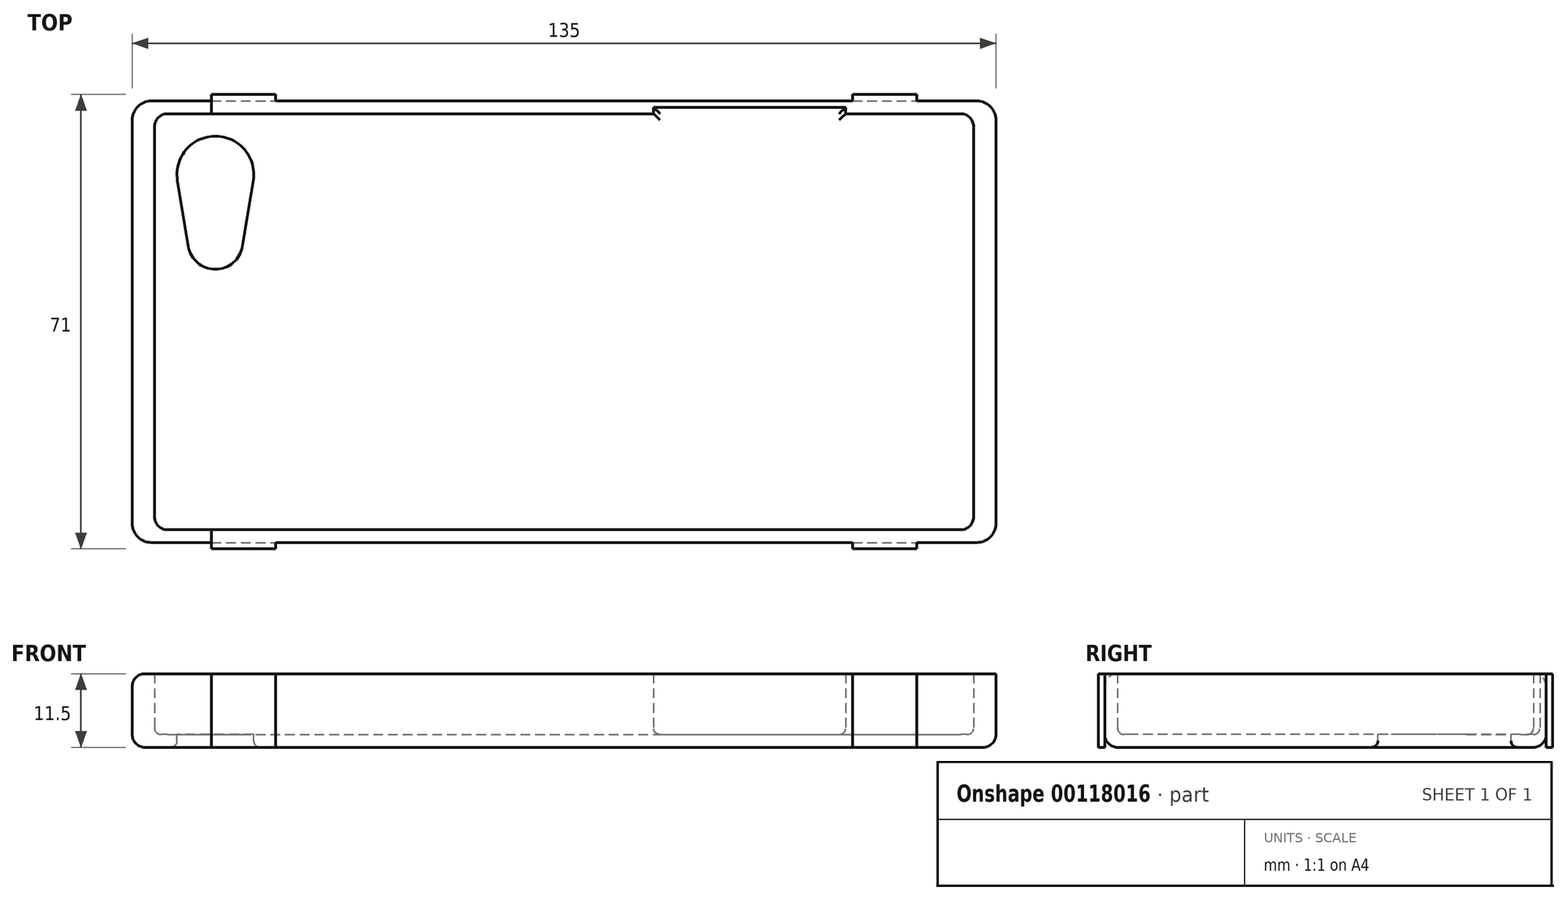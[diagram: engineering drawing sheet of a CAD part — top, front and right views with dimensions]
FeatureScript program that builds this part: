
annotation { "Feature Type Name" : "Feature", "Feature Type Description" : "" }
export const myFeature = defineFeature(function(context is Context, id is Id, definition is map)
    precondition{}
    {
        {
            var Q0;
            Q0=qCreatedBy(makeId("Top.planeOp"),FACE);
            var sketch = newSketch(context, id + "F0", { "sketchPlane" : qUnion([Q0])});
            skLineSegment(sketch, "E0.bottom", {"start": v(-67.5, 34.5) * mm, "end": v(67.5, 34.5) * mm});
            skLineSegment(sketch, "E0.top", {"start": v(-67.5, -34.5) * mm, "end": v(67.5, -34.5) * mm});
            skLineSegment(sketch, "E0.left", {"start": v(-67.5, 34.5) * mm, "end": v(-67.5, -34.5) * mm});
            skLineSegment(sketch, "E0.right", {"start": v(67.5, 34.5) * mm, "end": v(67.5, -34.5) * mm});
            skLineSegment(sketch, "E1.bottom", {"start": v(-64, 32.5) * mm, "end": v(14, 32.5) * mm});
            skLineSegment(sketch, "E1.top", {"start": v(-64, -32.5) * mm, "end": v(64, -32.5) * mm});
            skLineSegment(sketch, "E1.left", {"start": v(-64, 32.5) * mm, "end": v(-64, -32.5) * mm});
            skLineSegment(sketch, "E1.right", {"start": v(64, 32.5) * mm, "end": v(64, -32.5) * mm});
            skLineSegment(sketch, "E2", {"start": v(14, 32.5) * mm, "end": v(14, 33.5) * mm});
            skLineSegment(sketch, "E3", {"start": v(14, 33.5) * mm, "end": v(44, 33.5) * mm});
            skLineSegment(sketch, "E4", {"start": v(44, 33.5) * mm, "end": v(44, 32.5) * mm});
            skLineSegment(sketch, "E5.trimOffspring", {"start": v(44, 32.5) * mm, "end": v(64, 32.5) * mm});
            skSolve(sketch);
        }
        {
            var Q0;
            Q0=makeQuery(id+"F0.imprint","IMPRINT",FACE,{"disambiguationData":[TD([[makeQuery(id+"F0.imprint","IMPRINT",EDGE,{"derivedFrom":sQuery(id+"F0.wireOp",EDGE,"E0.bottom")}),-1.0]])]});
            extrude(context, id + "F1", {"entities" : qUnion([Q0]), "depth" : 11.5 * mm});
        }
        {
            var Q0;
            Q0=makeQuery(id+"F0.imprint","IMPRINT",FACE,{"disambiguationData":[TD([[makeQuery(id+"F0.imprint","IMPRINT",EDGE,{"derivedFrom":sQuery(id+"F0.wireOp",EDGE,"E1.bottom")}),-1.0]])]});
            extrude(context, id + "F2", {"entities" : qUnion([Q0]), "operationType" : NewBodyOperationType.ADD, "depth" : 2 * mm});
        }
        {
            var Q0;
            {var subQ0=sQuery(id+"F0.wireOp",EDGE,"E5.trimOffspring");var subQ1=sQuery(id+"F0.wireOp",EDGE,"E4");var subQ2=sQuery(id+"F0.wireOp",EDGE,"E3");var subQ3=sQuery(id+"F0.wireOp",EDGE,"E2");var subQ4=sQuery(id+"F0.wireOp",EDGE,"E1.right");var subQ5=sQuery(id+"F0.wireOp",EDGE,"E1.left");var subQ6=sQuery(id+"F0.wireOp",EDGE,"E1.top");var subQ7=sQuery(id+"F0.wireOp",EDGE,"E1.bottom");Q0=makeQuery(id+"F2.boolean.opBoolean","MERGE",FACE,{"derivedFrom":[makeQuery(id+"F1.opExtrude","CAP_FACE",FACE,{"disambiguationData":[OSD([sQuery(id+"F0.wireOp",EDGE,"E0.bottom"),sQuery(id+"F0.wireOp",EDGE,"E0.top"),sQuery(id+"F0.wireOp",EDGE,"E0.left"),sQuery(id+"F0.wireOp",EDGE,"E0.right"),subQ7,subQ6,subQ5,subQ4,subQ3,subQ2,subQ1,subQ0])],"isStart":true}),makeQuery(id+"F2.opExtrude","CAP_FACE",FACE,{"disambiguationData":[OSD([subQ7,subQ6,subQ5,subQ4,subQ3,subQ2,subQ1,subQ0])],"isStart":true})]});}
            fillet(context, id + "F3", {"entities" : qUnion([Q0]), "radius" : 2 * mm, "tangentPropagation" : true, "allowEdgeOverflow" : false});
        }
        {
            var Q0;
            Q0=makeQuery(id+"F1.opExtrude","SWEPT_EDGE",EDGE,{"disambiguationData":[OSD([sQuery(id+"F0.wireOp",EDGE,"E1.bottom"),sQuery(id+"F0.wireOp",EDGE,"E1.left")])]});
            var Q1;
            Q1=makeQuery(id+"F1.opExtrude","SWEPT_EDGE",EDGE,{"disambiguationData":[OSD([sQuery(id+"F0.wireOp",EDGE,"E1.right"),sQuery(id+"F0.wireOp",EDGE,"E5.trimOffspring")])]});
            var Q2;
            Q2=makeQuery(id+"F1.opExtrude","SWEPT_EDGE",EDGE,{"disambiguationData":[OSD([sQuery(id+"F0.wireOp",EDGE,"E1.top"),sQuery(id+"F0.wireOp",EDGE,"E1.right")])]});
            var Q3;
            Q3=makeQuery(id+"F1.opExtrude","SWEPT_EDGE",EDGE,{"disambiguationData":[OSD([sQuery(id+"F0.wireOp",EDGE,"E1.top"),sQuery(id+"F0.wireOp",EDGE,"E1.left")])]});
            fillet(context, id + "F4", {"entities" : qUnion([Q0, Q1, Q2, Q3]), "radius" : 2 * mm, "tangentPropagation" : true, "allowEdgeOverflow" : false});
        }
        {
            var Q0;
            Q0=makeQuery(id+"F2.opExtrude","CAP_FACE",FACE,{"disambiguationData":[OSD([sQuery(id+"F0.wireOp",EDGE,"E1.bottom"),sQuery(id+"F0.wireOp",EDGE,"E1.top"),sQuery(id+"F0.wireOp",EDGE,"E1.left"),sQuery(id+"F0.wireOp",EDGE,"E1.right"),sQuery(id+"F0.wireOp",EDGE,"E2"),sQuery(id+"F0.wireOp",EDGE,"E3"),sQuery(id+"F0.wireOp",EDGE,"E4"),sQuery(id+"F0.wireOp",EDGE,"E5.trimOffspring")])],"isStart":false});
            fillet(context, id + "F5", {"entities" : qUnion([Q0]), "radius" : 1 * mm, "tangentPropagation" : true, "allowEdgeOverflow" : false});
        }
        {
            var Q0;
            Q0=makeQuery(id+"F1.opExtrude","SWEPT_EDGE",EDGE,{"disambiguationData":[OSD([sQuery(id+"F0.wireOp",EDGE,"E0.bottom"),sQuery(id+"F0.wireOp",EDGE,"E0.left")])]});
            var Q1;
            Q1=makeQuery(id+"F1.opExtrude","SWEPT_EDGE",EDGE,{"disambiguationData":[OSD([sQuery(id+"F0.wireOp",EDGE,"E0.top"),sQuery(id+"F0.wireOp",EDGE,"E0.left")])]});
            var Q2;
            Q2=makeQuery(id+"F1.opExtrude","SWEPT_EDGE",EDGE,{"disambiguationData":[OSD([sQuery(id+"F0.wireOp",EDGE,"E0.top"),sQuery(id+"F0.wireOp",EDGE,"E0.right")])]});
            var Q3;
            Q3=makeQuery(id+"F1.opExtrude","SWEPT_EDGE",EDGE,{"disambiguationData":[OSD([sQuery(id+"F0.wireOp",EDGE,"E0.bottom"),sQuery(id+"F0.wireOp",EDGE,"E0.right")])]});
            fillet(context, id + "F6", {"entities" : qUnion([Q0, Q1, Q2, Q3]), "radius" : 3 * mm, "tangentPropagation" : true, "allowEdgeOverflow" : false});
        }
        {
            var Q0;
            Q0=makeQuery(id+"F1.opExtrude","CAP_FACE",FACE,{"disambiguationData":[OSD([sQuery(id+"F0.wireOp",EDGE,"E0.bottom"),sQuery(id+"F0.wireOp",EDGE,"E0.top"),sQuery(id+"F0.wireOp",EDGE,"E0.left"),sQuery(id+"F0.wireOp",EDGE,"E0.right"),sQuery(id+"F0.wireOp",EDGE,"E1.bottom"),sQuery(id+"F0.wireOp",EDGE,"E1.top"),sQuery(id+"F0.wireOp",EDGE,"E1.left"),sQuery(id+"F0.wireOp",EDGE,"E1.right"),sQuery(id+"F0.wireOp",EDGE,"E2"),sQuery(id+"F0.wireOp",EDGE,"E3"),sQuery(id+"F0.wireOp",EDGE,"E4"),sQuery(id+"F0.wireOp",EDGE,"E5.trimOffspring")])],"isStart":false});
            var sketch = newSketch(context, id + "F7", { "sketchPlane" : qUnion([Q0])});
            skLineSegment(sketch, "E6", {"start": v(-55.1, 34.5) * mm, "end": v(-55.1, 35.5) * mm});
            skLineSegment(sketch, "E7", {"start": v(-55.1, 35.5) * mm, "end": v(-45.1, 35.5) * mm});
            skLineSegment(sketch, "E8", {"start": v(-45.1, 35.5) * mm, "end": v(-45.1, 34.5) * mm});
            skLineSegment(sketch, "E9.MirrorCS", {"start": v(55.1, 35.5) * mm, "end": v(45.1, 35.5) * mm});
            skLineSegment(sketch, "E10.MirrorCS", {"start": v(45.1, 35.5) * mm, "end": v(45.1, 34.5) * mm});
            skLineSegment(sketch, "E11.MirrorCS", {"start": v(55.1, 34.5) * mm, "end": v(55.1, 35.5) * mm});
            skLineSegment(sketch, "E12.MirrorCS", {"start": v(-45.1, -35.5) * mm, "end": v(-45.1, -34.5) * mm});
            skLineSegment(sketch, "E13.MirrorCS", {"start": v(55.1, -34.5) * mm, "end": v(55.1, -35.5) * mm});
            skLineSegment(sketch, "E14.MirrorCS", {"start": v(45.1, -35.5) * mm, "end": v(45.1, -34.5) * mm});
            skLineSegment(sketch, "E15.MirrorCS", {"start": v(-55.1, -34.5) * mm, "end": v(-55.1, -35.5) * mm});
            skLineSegment(sketch, "E16.MirrorCS", {"start": v(55.1, -35.5) * mm, "end": v(45.1, -35.5) * mm});
            skLineSegment(sketch, "E17.MirrorCS", {"start": v(-55.1, -35.5) * mm, "end": v(-45.1, -35.5) * mm});
            skLineSegment(sketch, "E18", {"start": v(-55.1, 34.5) * mm, "end": v(-45.1, 34.5) * mm});
            skLineSegment(sketch, "E19", {"start": v(45.1, 34.5) * mm, "end": v(55.1, 34.5) * mm});
            skLineSegment(sketch, "E20", {"start": v(-55.1, -34.5) * mm, "end": v(-45.1, -34.5) * mm});
            skLineSegment(sketch, "E21", {"start": v(45.1, -34.5) * mm, "end": v(55.1, -34.5) * mm});
            skSolve(sketch);
        }
        {
            var Q0;
            Q0 = qSketchRegion(id + "F7", true);
            var Q1;
            {var subQ0=sQuery(id+"F0.wireOp",EDGE,"E5.trimOffspring");var subQ1=sQuery(id+"F0.wireOp",EDGE,"E4");var subQ2=sQuery(id+"F0.wireOp",EDGE,"E3");var subQ3=sQuery(id+"F0.wireOp",EDGE,"E2");var subQ4=sQuery(id+"F0.wireOp",EDGE,"E1.right");var subQ5=sQuery(id+"F0.wireOp",EDGE,"E1.left");var subQ6=sQuery(id+"F0.wireOp",EDGE,"E1.top");var subQ7=sQuery(id+"F0.wireOp",EDGE,"E1.bottom");Q1=makeQuery(id+"F2.boolean.opBoolean","MERGE",FACE,{"derivedFrom":[makeQuery(id+"F1.opExtrude","CAP_FACE",FACE,{"disambiguationData":[OSD([sQuery(id+"F0.wireOp",EDGE,"E0.bottom"),sQuery(id+"F0.wireOp",EDGE,"E0.top"),sQuery(id+"F0.wireOp",EDGE,"E0.left"),sQuery(id+"F0.wireOp",EDGE,"E0.right"),subQ7,subQ6,subQ5,subQ4,subQ3,subQ2,subQ1,subQ0])],"isStart":true}),makeQuery(id+"F2.opExtrude","CAP_FACE",FACE,{"disambiguationData":[OSD([subQ7,subQ6,subQ5,subQ4,subQ3,subQ2,subQ1,subQ0])],"isStart":true})]});}
            extrude(context, id + "F8", {"entities" : qUnion([Q0]), "operationType" : NewBodyOperationType.ADD, "endBound" : BoundingType.UP_TO_SURFACE, "oppositeDirection" : true, "endBoundEntityFace" : qUnion([Q1]), "depth" : 25 * mm});
        }
        {
            var Q0;
            Q0=makeQuery(id+"F2.opExtrude","CAP_FACE",FACE,{"disambiguationData":[OSD([sQuery(id+"F0.wireOp",EDGE,"E1.bottom"),sQuery(id+"F0.wireOp",EDGE,"E1.top"),sQuery(id+"F0.wireOp",EDGE,"E1.left"),sQuery(id+"F0.wireOp",EDGE,"E1.right"),sQuery(id+"F0.wireOp",EDGE,"E2"),sQuery(id+"F0.wireOp",EDGE,"E3"),sQuery(id+"F0.wireOp",EDGE,"E4"),sQuery(id+"F0.wireOp",EDGE,"E5.trimOffspring")])],"isStart":false});
            var sketch = newSketch(context, id + "F9", { "sketchPlane" : qUnion([Q0])});
            skArc(sketch, "E22", {"start": v(-48.58, 22.03) * mm, "mid": v(-54.5, 29) * mm, "end": v(-60.42, 22.03) * mm});
            skArc(sketch, "E23", {"start": v(-58.74, 11.8) * mm, "mid": v(-54.5, 8.2) * mm, "end": v(-50.26, 11.8) * mm});
            skLineSegment(sketch, "E24", {"start": v(-48.58, 22.03) * mm, "end": v(-50.26, 11.8) * mm});
            skLineSegment(sketch, "E25", {"start": v(-60.42, 22.03) * mm, "end": v(-58.74, 11.8) * mm});
            skSolve(sketch);
        }
        {
            var Q0;
            Q0 = qSketchRegion(id + "F9", true);
            extrude(context, id + "F10", {"entities" : qUnion([Q0]), "operationType" : NewBodyOperationType.REMOVE, "oppositeDirection" : true, "depth" : 25 * mm});
        }
        {
            var Q0;
            Q0=makeQuery(id+"F10.boolean.opBoolean","COPY",EDGE,{"derivedFrom":makeQuery(id+"F10.opExtrude","CAP_EDGE",EDGE,{"disambiguationData":[OSD([sQuery(id+"F9.wireOp",EDGE,"E22")])],"isStart":true})});
            var Q1;
            {var subQ0=sQuery(id+"F0.wireOp",EDGE,"E5.trimOffspring");var subQ1=sQuery(id+"F0.wireOp",EDGE,"E4");var subQ2=sQuery(id+"F0.wireOp",EDGE,"E3");var subQ3=sQuery(id+"F0.wireOp",EDGE,"E2");var subQ4=sQuery(id+"F0.wireOp",EDGE,"E1.right");var subQ5=sQuery(id+"F0.wireOp",EDGE,"E1.left");var subQ6=sQuery(id+"F0.wireOp",EDGE,"E1.top");var subQ7=sQuery(id+"F0.wireOp",EDGE,"E1.bottom");Q1=makeQuery(id+"F10.boolean.opBoolean","INTERSECT",EDGE,{"derivedFrom":[makeQuery(id+"F2.boolean.opBoolean","MERGE",FACE,{"derivedFrom":[makeQuery(id+"F1.opExtrude","CAP_FACE",FACE,{"disambiguationData":[OSD([sQuery(id+"F0.wireOp",EDGE,"E0.bottom"),sQuery(id+"F0.wireOp",EDGE,"E0.top"),sQuery(id+"F0.wireOp",EDGE,"E0.left"),sQuery(id+"F0.wireOp",EDGE,"E0.right"),subQ7,subQ6,subQ5,subQ4,subQ3,subQ2,subQ1,subQ0])],"isStart":true}),makeQuery(id+"F2.opExtrude","CAP_FACE",FACE,{"disambiguationData":[OSD([subQ7,subQ6,subQ5,subQ4,subQ3,subQ2,subQ1,subQ0])],"isStart":true})]}),makeQuery(id+"F10.opExtrude","SWEPT_FACE",FACE,{"disambiguationData":[OSD([sQuery(id+"F9.wireOp",EDGE,"E24")])]})]});}
            fillet(context, id + "F11", {"entities" : qUnion([Q0, Q1]), "radius" : 1 * mm, "tangentPropagation" : true, "allowEdgeOverflow" : false});
        }
        {
            var Q0;
            Q0=makeQuery(id+"F1.opExtrude","CAP_EDGE",EDGE,{"disambiguationData":[OSD([sQuery(id+"F0.wireOp",EDGE,"E0.left")])],"isStart":false});
            fillet(context, id + "F12", {"entities" : qUnion([Q0]), "radius" : 2 * mm, "tangentPropagation" : true, "allowEdgeOverflow" : false});
        }
    });
